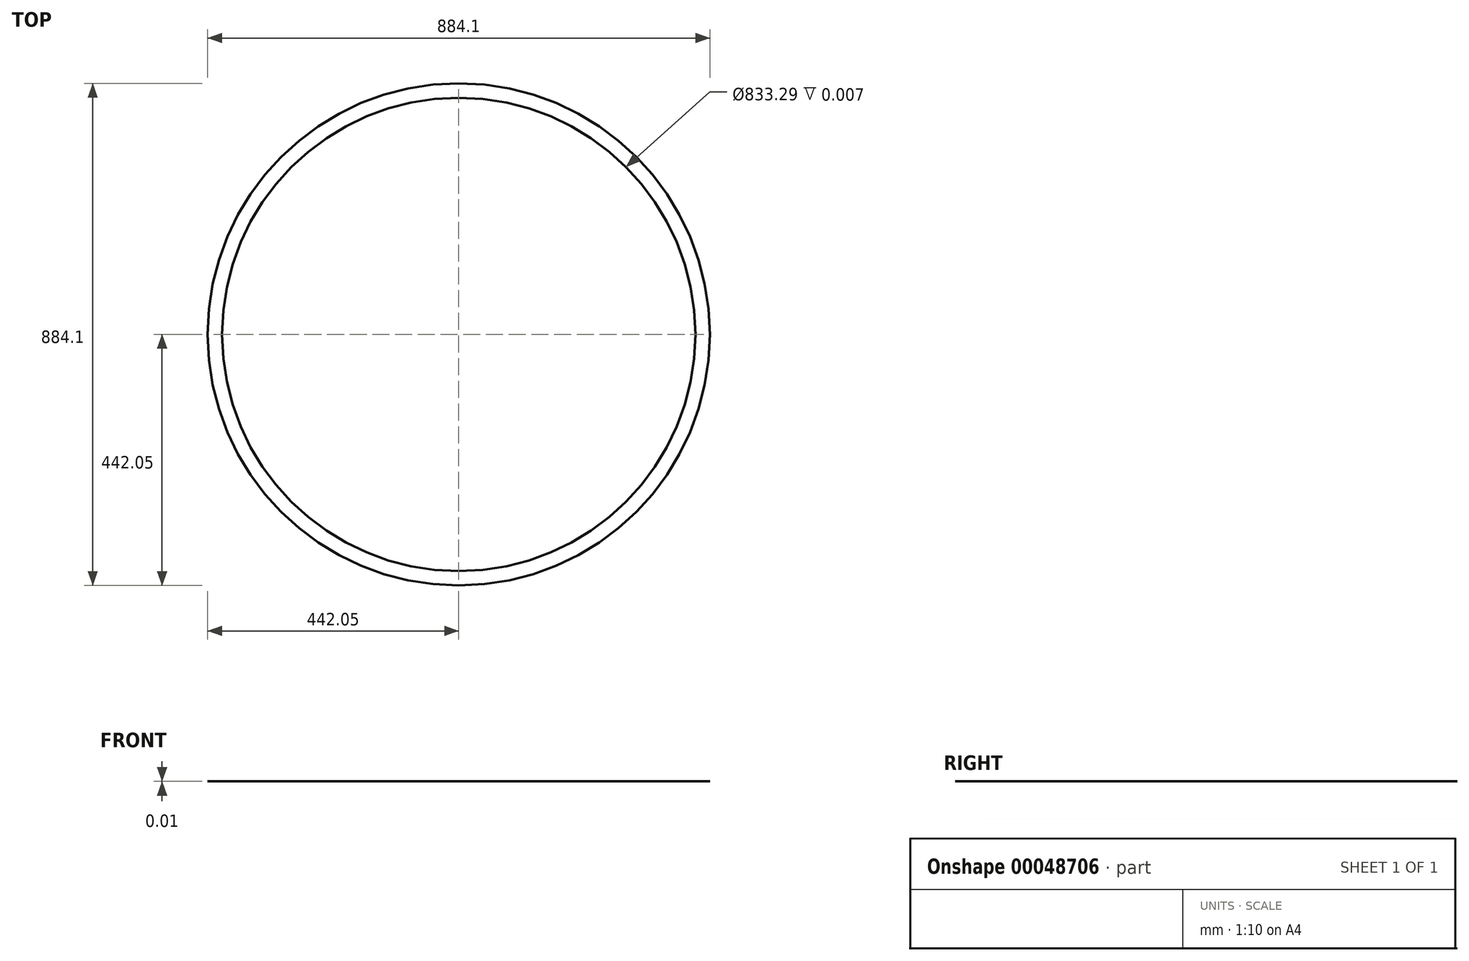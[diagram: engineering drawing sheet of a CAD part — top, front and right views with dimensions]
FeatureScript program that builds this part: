
annotation { "Feature Type Name" : "Feature", "Feature Type Description" : "" }
export const myFeature = defineFeature(function(context is Context, id is Id, definition is map)
    precondition{}
    {
        {
            var Q0;
            Q0=qCreatedBy(makeId("Top.planeOp"),FACE);
            var sketch = newSketch(context, id + "F0", { "sketchPlane" : qUnion([Q0])});
            skCircle(sketch, "E0", {"center": v(0, 0) * mm, "radius": 442.05 * mm});
            skCircle(sketch, "E1", {"center": v(0, 0) * mm, "radius": 416.65 * mm});
            skSolve(sketch);
        }
        {
            var Q0;
            Q0 = qSketchRegion(id + "F0", true);
            extrude(context, id + "F1", {"entities" : qUnion([Q0]), "depth" : 3 / 457.2 * mm});
        }
    });
